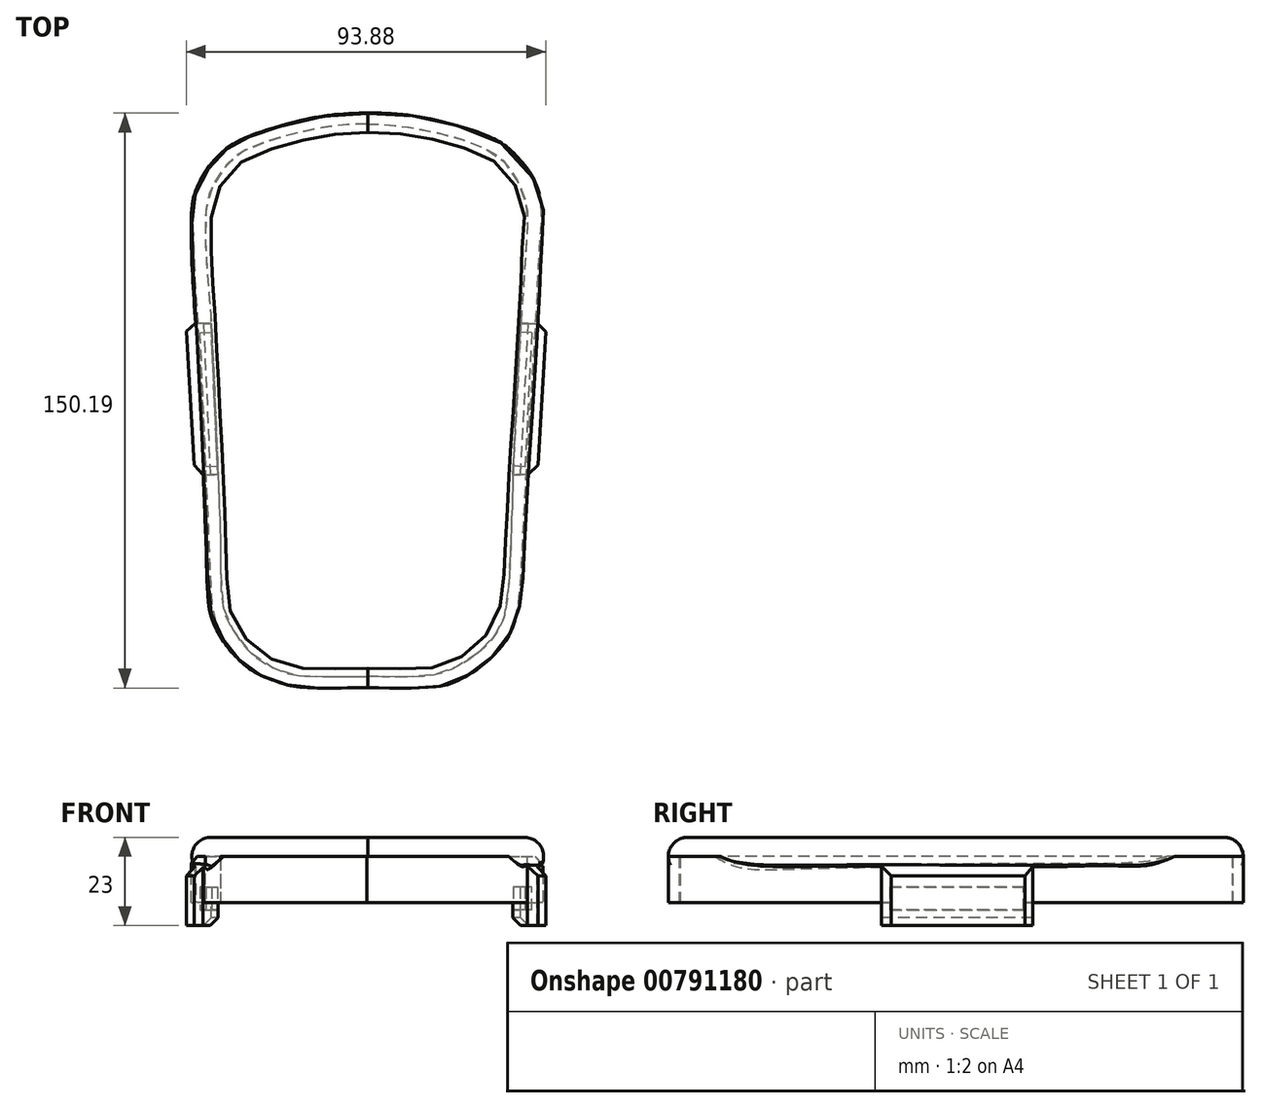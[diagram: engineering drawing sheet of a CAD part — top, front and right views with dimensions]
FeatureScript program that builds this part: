
annotation { "Feature Type Name" : "Feature", "Feature Type Description" : "" }
export const myFeature = defineFeature(function(context is Context, id is Id, definition is map)
    precondition{}
    {
        {
            var Q0;
            Q0=qCreatedBy(makeId("Top.planeOp"),FACE);
            var sketch = newSketch(context, id + "F0", { "sketchPlane" : qUnion([Q0])});
            skFitSpline(sketch, "E0", {"points": [v(0, 54.28) * mm, v(-7.64, 53.94) * mm, v(-16.8, 52.44) * mm, v(-27.76, 49.31) * mm, v(-35.75, 45.74) * mm, v(-41.54, 39.87) * mm, v(-45.26, 32.29) * mm, v(-45.92, 23.61) * mm, v(-45.66, 14.25) * mm, v(-44.79, -0.63) * mm, v(-42.01, -59.14) * mm, v(-41.15, -75.2) * mm, v(-39.2, -80.84) * mm, v(-35.2, -86.6) * mm, v(-30.98, -90.64) * mm, v(-26.93, -92.91) * mm, v(-21.48, -94.87) * mm, v(-16.82, -95.67) * mm, v(0, -95.72) * mm], "startDerivative": vector(-157.53, -3.33) * mm, "endDerivative": vector(276.88, 4.26) * mm});
            skFitSpline(sketch, "E1", {"points": [v(0, 54.28) * mm, v(7.23, 54.1) * mm, v(16.87, 52.7) * mm, v(26.1, 50.23) * mm, v(32.08, 48.02) * mm, v(37.15, 44.8) * mm, v(41.87, 39.48) * mm, v(44.47, 34.64) * mm, v(45.9, 28.63) * mm, v(45.39, 19.41) * mm, v(44.8, 6.04) * mm, v(41.57, -46.32) * mm, v(40.23, -70.34) * mm, v(38.38, -79) * mm, v(34.56, -85.4) * mm, v(29.97, -89.9) * mm, v(24.06, -93.65) * mm, v(18.48, -95.4) * mm, v(0, -95.72) * mm], "startDerivative": vector(149.89, 0.1) * mm, "endDerivative": vector(-287.35, 5.18) * mm});
            skPoint(sketch, "E2", {"position": v(-42.75, -40.42) * mm});
            skPoint(sketch, "E3", {"position": v(41.92, -40.28) * mm});
            skPoint(sketch, "E4", {"position": v(-38.92, -40.2) * mm});
            skPoint(sketch, "E5", {"position": v(38.13, -39.98) * mm});
            skPoint(sketch, "E6", {"position": v(-40.67, -0.9) * mm});
            skPoint(sketch, "E7", {"position": v(40.13, -1.07) * mm});
            skFitSpline(sketch, "E8", {"points": [v(0, 51.39) * mm, v(-4.34, 51.3) * mm, v(-11.2, 50.52) * mm, v(-20.47, 48.53) * mm, v(-27.92, 46.19) * mm, v(-33.47, 43.58) * mm, v(-37.55, 39.6) * mm, v(-40.93, 33.87) * mm, v(-42.14, 27.55) * mm, v(-42.05, 17.4) * mm, v(-40.67, -0.9) * mm, v(-38.92, -40.2) * mm, v(-38.24, -59.4) * mm, v(-37.46, -75.44) * mm, v(-34.51, -81.51) * mm, v(-29.66, -87.4) * mm, v(-21.5, -91.83) * mm, v(-15.79, -92.78) * mm, v(0, -92.87) * mm], "startDerivative": vector(-114.24, 0.07) * mm, "endDerivative": vector(260.7, 1.93) * mm});
            skFitSpline(sketch, "E9", {"points": [v(0, 51.39) * mm, v(3.19, 51.39) * mm, v(10.5, 50.61) * mm, v(21.95, 48.24) * mm, v(28.75, 45.87) * mm, v(34.53, 42.78) * mm, v(39.06, 36.9) * mm, v(41.54, 30.61) * mm, v(41.74, 22.78) * mm, v(40.13, -1.07) * mm, v(38.13, -39.98) * mm, v(36.28, -75.27) * mm, v(34.33, -80.63) * mm, v(30.61, -85.37) * mm, v(23.08, -90.52) * mm, v(16.18, -92.69) * mm, v(0, -92.87) * mm], "startDerivative": vector(86.43, 2.25) * mm, "endDerivative": vector(-237.55, 7.6) * mm});
            skLineSegment(sketch, "E10", {"start": v(0, -127.63) * mm, "end": v(0, 92.1) * mm, "construction": true});
            skSolve(sketch);
        }
        {
            var Q0;
            Q0 = qSketchRegion(id + "F0", true);
            extrude(context, id + "F1", {"entities" : qUnion([Q0]), "depth" : 12 * mm, "offsetDistance" : 25 * mm});
        }
        {
            var Q0;
            Q0=makeQuery(id+"F1.opExtrude","CAP_FACE",FACE,{"disambiguationData":[OSD([sQuery(id+"F0.wireOp",EDGE,"E0"),sQuery(id+"F0.wireOp",EDGE,"E1"),sQuery(id+"F0.wireOp",EDGE,"E8"),sQuery(id+"F0.wireOp",EDGE,"E9")])],"isStart":false});
            var sketch = newSketch(context, id + "F2", { "sketchPlane" : qUnion([Q0])});
            skFitSpline(sketch, "E11", {"points": [v(0.19, 54.2) * mm, v(-7.46, 53.86) * mm, v(-16.6, 52.37) * mm, v(-27.58, 49.23) * mm, v(-35.56, 45.66) * mm, v(-41.35, 39.8) * mm, v(-45.07, 32.2) * mm, v(-45.73, 23.53) * mm, v(-45.47, 14.17) * mm, v(-44.6, -0.7) * mm, v(-41.82, -59.22) * mm, v(-40.96, -75.28) * mm, v(-39, -80.92) * mm, v(-35.02, -86.68) * mm, v(-30.79, -90.72) * mm, v(-26.74, -93) * mm, v(-21.29, -94.95) * mm, v(-16.63, -95.75) * mm, v(0.19, -95.8) * mm], "startDerivative": vector(-157.53, -3.33) * mm, "endDerivative": vector(276.88, 4.26) * mm});
            skFitSpline(sketch, "E12", {"points": [v(0.19, 54.2) * mm, v(7.42, 54.02) * mm, v(17.06, 52.63) * mm, v(26.28, 50.15) * mm, v(32.26, 47.94) * mm, v(37.34, 44.71) * mm, v(42.06, 39.4) * mm, v(44.66, 34.56) * mm, v(46.09, 28.55) * mm, v(45.58, 19.33) * mm, v(45, 5.96) * mm, v(41.76, -46.4) * mm, v(40.42, -70.42) * mm, v(38.57, -79.08) * mm, v(34.75, -85.47) * mm, v(30.15, -89.98) * mm, v(24.25, -93.73) * mm, v(18.67, -95.48) * mm, v(0.19, -95.8) * mm], "startDerivative": vector(149.89, 0.1) * mm, "endDerivative": vector(-287.35, 5.18) * mm});
            skSolve(sketch);
        }
        {
            var Q0;
            Q0 = qSketchRegion(id + "F2", true);
            extrude(context, id + "F3", {"entities" : qUnion([Q0]), "operationType" : NewBodyOperationType.ADD, "depth" : 5 * mm, "offsetDistance" : 25 * mm});
        }
        {
            var Q0;
            Q0=makeQuery(id+"F3.opExtrude","CAP_EDGE",EDGE,{"disambiguationData":[OSD([sQuery(id+"F2.wireOp",EDGE,"E11")])],"isStart":false});
            var Q1;
            Q1=makeQuery(id+"F3.opExtrude","CAP_EDGE",EDGE,{"disambiguationData":[OSD([sQuery(id+"F2.wireOp",EDGE,"E12")])],"isStart":false});
            fillet(context, id + "F4", {"entities" : qUnion([Q0, Q1]), "radius" : 5 * mm, "tangentPropagation" : true, "allowEdgeOverflow" : false});
        }
        {
            var Q0;
            Q0=makeQuery(id+"F1.opExtrude","CAP_FACE",FACE,{"disambiguationData":[OSD([sQuery(id+"F0.wireOp",EDGE,"E0"),sQuery(id+"F0.wireOp",EDGE,"E1"),sQuery(id+"F0.wireOp",EDGE,"E8"),sQuery(id+"F0.wireOp",EDGE,"E9")])],"isStart":true});
            var sketch = newSketch(context, id + "F5", { "sketchPlane" : qUnion([Q0])});
            skLineSegment(sketch, "E13", {"start": v(40.15, 0.7) * mm, "end": v(44.44, 0.7) * mm});
            skLineSegment(sketch, "E14", {"start": v(44.44, 0.7) * mm, "end": v(46.68, 2.79) * mm});
            skLineSegment(sketch, "E15", {"start": v(46.68, 2.79) * mm, "end": v(44.62, 37.66) * mm});
            skLineSegment(sketch, "E16", {"start": v(44.62, 37.66) * mm, "end": v(41.92, 40.23) * mm});
            skLineSegment(sketch, "E17", {"start": v(41.92, 40.23) * mm, "end": v(38.12, 40.23) * mm});
            skLineSegment(sketch, "E18", {"start": v(38.12, 40.23) * mm, "end": v(40.15, 0.7) * mm});
            skLineSegment(sketch, "E19.MirrorCS", {"start": v(-40.68, 0.7) * mm, "end": v(-44.89, 0.7) * mm});
            skLineSegment(sketch, "E20.MirrorCS", {"start": v(-47.2, 2.79) * mm, "end": v(-45.15, 37.66) * mm});
            skLineSegment(sketch, "E21.MirrorCS", {"start": v(-45.15, 37.66) * mm, "end": v(-42.85, 40.23) * mm});
            skLineSegment(sketch, "E22.MirrorCS", {"start": v(-38.92, 40.23) * mm, "end": v(-40.68, 0.7) * mm});
            skLineSegment(sketch, "E23.MirrorCS", {"start": v(-44.89, 0.7) * mm, "end": v(-47.2, 2.79) * mm});
            skLineSegment(sketch, "E24.MirrorCS", {"start": v(-42.85, 40.23) * mm, "end": v(-38.92, 40.23) * mm});
            skLineSegment(sketch, "E25", {"start": v(38.12, 40.23) * mm, "end": v(-49.3, 40.23) * mm, "construction": true});
            skLineSegment(sketch, "E26", {"start": v(40.15, 0.7) * mm, "end": v(-53.51, 0.7) * mm, "construction": true});
            skSolve(sketch);
        }
        {
            var Q0;
            Q0 = qSketchRegion(id + "F5", true);
            extrude(context, id + "F6", {"entities" : qUnion([Q0]), "operationType" : NewBodyOperationType.ADD, "depth" : 6 * mm, "offsetDistance" : 25 * mm, "hasSecondDirection" : true, "secondDirectionOppositeDirection" : true, "secondDirectionDepth" : 12 * mm});
        }
        {
            var Q0;
            Q0=makeQuery(id+"F6.opExtrude","CAP_EDGE",EDGE,{"disambiguationData":[OSD([sQuery(id+"F5.wireOp",EDGE,"E15")])],"isStart":true});
            chamfer(context, id + "F7", {"entities" : qUnion([Q0]), "width" : 5 * mm, "tangentPropagation" : true});
        }
        {
            var Q0;
            Q0=makeQuery(id+"F6.opExtrude","CAP_EDGE",EDGE,{"disambiguationData":[OSD([sQuery(id+"F5.wireOp",EDGE,"E18")])],"isStart":false});
            chamfer(context, id + "F8", {"entities" : qUnion([Q0]), "width" : 2 * mm, "tangentPropagation" : true});
        }
        {
            var Q0;
            Q0=makeQuery(id+"F6.opExtrude","SWEPT_FACE",FACE,{"disambiguationData":[OSD([sQuery(id+"F5.wireOp",EDGE,"E18")])]});
            var sketch = newSketch(context, id + "F9", { "sketchPlane" : qUnion([Q0])});
            skLineSegment(sketch, "E27.bottom", {"start": v(0.94, -2) * mm, "end": v(35.94, -2) * mm});
            skLineSegment(sketch, "E27.top", {"start": v(0.94, 4) * mm, "end": v(35.94, 4) * mm});
            skLineSegment(sketch, "E27.left", {"start": v(0.94, -2) * mm, "end": v(0.94, 4) * mm});
            skPoint(sketch, "E28", {"position": v(0.94, 0) * mm});
            skLineSegment(sketch, "E29", {"start": v(35.94, 4) * mm, "end": v(35.94, -2) * mm});
            skSolve(sketch);
        }
        {
            var Q0;
            Q0 = qSketchRegion(id + "F9", true);
            extrude(context, id + "F10", {"entities" : qUnion([Q0]), "operationType" : NewBodyOperationType.ADD, "oppositeDirection" : true, "depth" : 3 * mm, "offsetDistance" : 25 * mm, "hasSecondDirection" : true, "secondDirectionOppositeDirection" : false, "secondDirectionDepth" : 1 * mm});
        }
        {
            var Q0;
            Q0=makeQuery(id+"F6.opExtrude","CAP_EDGE",EDGE,{"disambiguationData":[OSD([sQuery(id+"F5.wireOp",EDGE,"E20.MirrorCS")])],"isStart":true});
            chamfer(context, id + "F11", {"entities" : qUnion([Q0]), "width" : 5 * mm, "tangentPropagation" : true});
        }
        {
            var Q0;
            Q0=makeQuery(id+"F6.opExtrude","CAP_EDGE",EDGE,{"disambiguationData":[OSD([sQuery(id+"F5.wireOp",EDGE,"E22.MirrorCS")])],"isStart":false});
            chamfer(context, id + "F12", {"entities" : qUnion([Q0]), "width" : 2 * mm, "tangentPropagation" : true});
        }
        {
            var Q0;
            Q0=makeQuery(id+"F6.opExtrude","SWEPT_FACE",FACE,{"disambiguationData":[OSD([sQuery(id+"F5.wireOp",EDGE,"E22.MirrorCS")])]});
            var sketch = newSketch(context, id + "F13", { "sketchPlane" : qUnion([Q0])});
            skLineSegment(sketch, "E30.bottom", {"start": v(-36.17, 4) * mm, "end": v(-1.17, 4) * mm});
            skLineSegment(sketch, "E30.top", {"start": v(-36.17, -2) * mm, "end": v(-1.17, -2) * mm});
            skLineSegment(sketch, "E30.left", {"start": v(-36.17, 4) * mm, "end": v(-36.17, -2) * mm});
            skLineSegment(sketch, "E30.right", {"start": v(-1.17, 4) * mm, "end": v(-1.17, -2) * mm});
            skPoint(sketch, "E31", {"position": v(-36.17, 0) * mm});
            skSolve(sketch);
        }
        {
            var Q0;
            Q0 = qSketchRegion(id + "F13", true);
            extrude(context, id + "F14", {"entities" : qUnion([Q0]), "operationType" : NewBodyOperationType.ADD, "oppositeDirection" : true, "depth" : 3 * mm, "offsetDistance" : 25 * mm, "hasSecondDirection" : true, "secondDirectionOppositeDirection" : false, "secondDirectionDepth" : 1 * mm});
        }
        {
            var Q0;
            Q0=makeQuery(id+"F14.opExtrude","CAP_FACE",FACE,{"disambiguationData":[OSD([sQuery(id+"F13.wireOp",EDGE,"E30.bottom"),sQuery(id+"F13.wireOp",EDGE,"E30.top"),sQuery(id+"F13.wireOp",EDGE,"E30.left"),sQuery(id+"F13.wireOp",EDGE,"E30.right")])],"isStart":true});
            extrude(context, id + "F15", {"entities" : qUnion([Q0]), "operationType" : NewBodyOperationType.REMOVE, "oppositeDirection" : true, "depth" : 4 * mm, "offsetDistance" : 25 * mm});
        }
        {
            var Q0;
            Q0=makeQuery(id+"F10.opExtrude","CAP_FACE",FACE,{"disambiguationData":[OSD([sQuery(id+"F9.wireOp",EDGE,"E27.bottom"),sQuery(id+"F9.wireOp",EDGE,"E27.top"),sQuery(id+"F9.wireOp",EDGE,"E27.left"),sQuery(id+"F9.wireOp",EDGE,"E29")])],"isStart":true});
            extrude(context, id + "F16", {"entities" : qUnion([Q0]), "operationType" : NewBodyOperationType.REMOVE, "oppositeDirection" : true, "depth" : 4 * mm, "offsetDistance" : 25 * mm});
        }
    });
